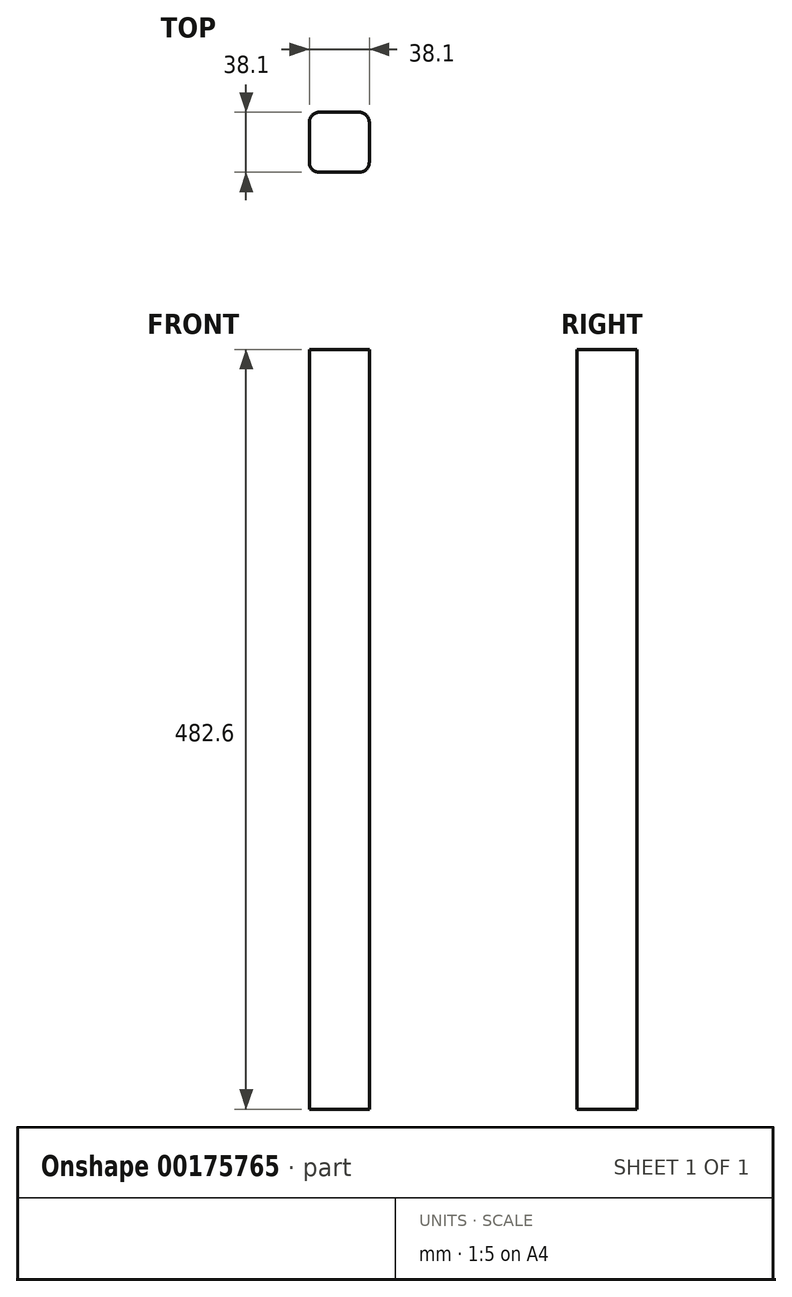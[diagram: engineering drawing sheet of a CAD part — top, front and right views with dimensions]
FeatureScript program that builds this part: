
annotation { "Feature Type Name" : "Feature", "Feature Type Description" : "" }
export const myFeature = defineFeature(function(context is Context, id is Id, definition is map)
    precondition{}
    {
        {
            var Q0;
            Q0=qCreatedBy(makeId("Top.planeOp"),FACE);
            var sketch = newSketch(context, id + "F0", { "sketchPlane" : qUnion([Q0])});
            skLineSegment(sketch, "E0.bottom", {"start": v(12.7, 19.05) * mm, "end": v(-12.7, 19.05) * mm});
            skLineSegment(sketch, "E0.top", {"start": v(12.7, -19.05) * mm, "end": v(-12.7, -19.05) * mm});
            skLineSegment(sketch, "E0.left", {"start": v(19.05, 12.7) * mm, "end": v(19.05, -12.7) * mm});
            skLineSegment(sketch, "E0.right", {"start": v(-19.05, 12.7) * mm, "end": v(-19.05, -12.7) * mm});
            skPoint(sketch, "E0.middle", {"position": v(0, 0) * mm});
            skPoint(sketch, "E1.visualSharp", {"position": v(-19.05, 19.05) * mm});
            skPoint(sketch, "E2.visualSharp", {"position": v(19.05, 19.05) * mm});
            skArc(sketch, "E2.filletArc", {"start": v(19.05, 12.7) * mm, "mid": v(17.2, 17.2) * mm, "end": v(12.7, 19.05) * mm});
            skPoint(sketch, "E3.visualSharp", {"position": v(19.05, -19.05) * mm});
            skArc(sketch, "E3.filletArc", {"start": v(12.7, -19.05) * mm, "mid": v(17.2, -17.2) * mm, "end": v(19.05, -12.7) * mm});
            skPoint(sketch, "E4.visualSharp", {"position": v(-19.05, -19.05) * mm});
            skArc(sketch, "E4.filletArc", {"start": v(-19.05, -12.7) * mm, "mid": v(-17.2, -17.2) * mm, "end": v(-12.7, -19.05) * mm});
            skArc(sketch, "E5.filletArc", {"start": v(-12.7, 19.05) * mm, "mid": v(-17.2, 17.2) * mm, "end": v(-19.05, 12.7) * mm});
            skSolve(sketch);
        }
        {
            var Q0;
            Q0=makeQuery(id+"F0.imprint","IMPRINT",FACE,{"disambiguationData":[TD([[makeQuery(id+"F0.imprint","IMPRINT",EDGE,{"derivedFrom":sQuery(id+"F0.wireOp",EDGE,"E0.bottom")}),1.0]])]});
            extrude(context, id + "F1", {"entities" : qUnion([Q0]), "depth" : 482.6 * mm, "offsetDistance" : 25.4 * mm});
        }
    });
